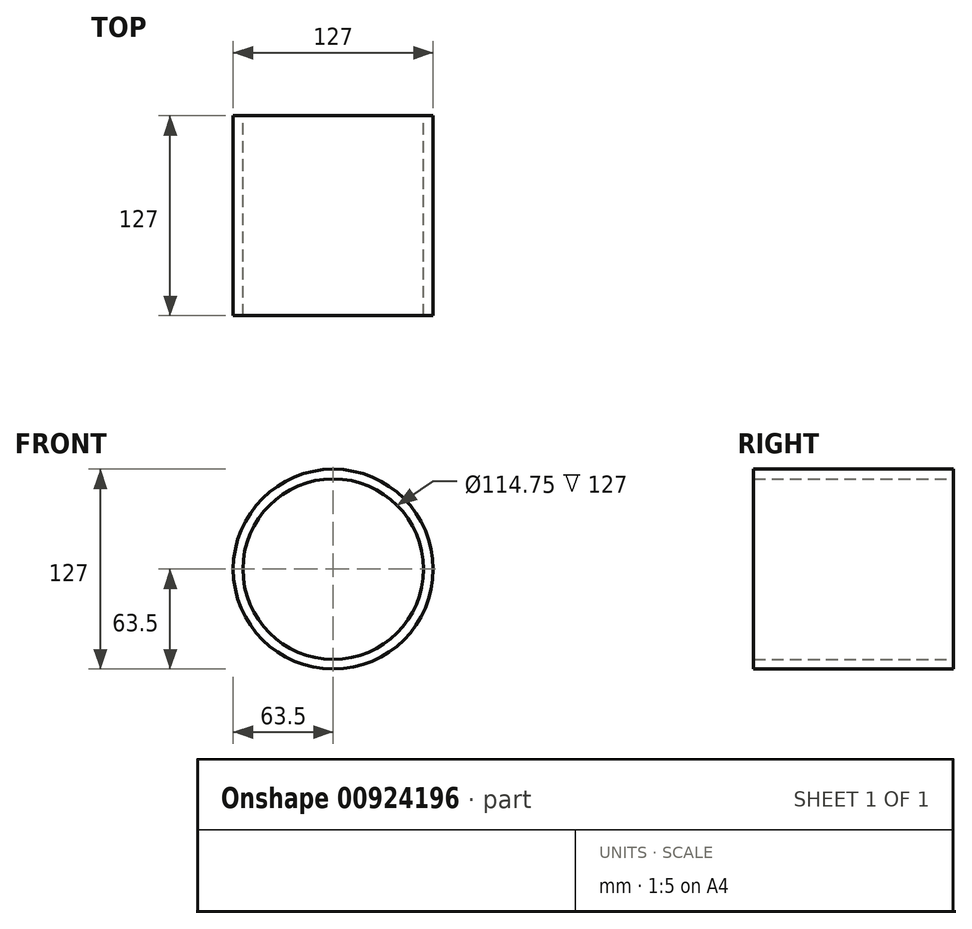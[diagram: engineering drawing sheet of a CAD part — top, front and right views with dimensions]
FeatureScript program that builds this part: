
annotation { "Feature Type Name" : "Feature", "Feature Type Description" : "" }
export const myFeature = defineFeature(function(context is Context, id is Id, definition is map)
    precondition{}
    {
        {
            var Q0;
            Q0=qCreatedBy(makeId("Front.planeOp"),FACE);
            var sketch = newSketch(context, id + "F0", { "sketchPlane" : qUnion([Q0])});
            skCircle(sketch, "E0", {"center": v(0, 0) * mm, "radius": 63.5 * mm});
            skCircle(sketch, "E1", {"center": v(0, 0) * mm, "radius": 57.37 * mm});
            skSolve(sketch);
        }
        {
            var Q0;
            Q0=makeQuery(id+"F0.imprint","IMPRINT",FACE,{"disambiguationData":[TD([[makeQuery(id+"F0.imprint","IMPRINT",EDGE,{"derivedFrom":sQuery(id+"F0.wireOp",EDGE,"E0")}),1.0]])]});
            var Q1;
            Q1=sQuery(id+"F0.wireOp",EDGE,"E0");
            extrude(context, id + "F1", {"entities" : qUnion([Q0]), "surfaceEntities" : qUnion([Q1]), "endBound" : BoundingType.SYMMETRIC, "depth" : 127 * mm, "offsetDistance" : 25.4 * mm});
        }
    });
